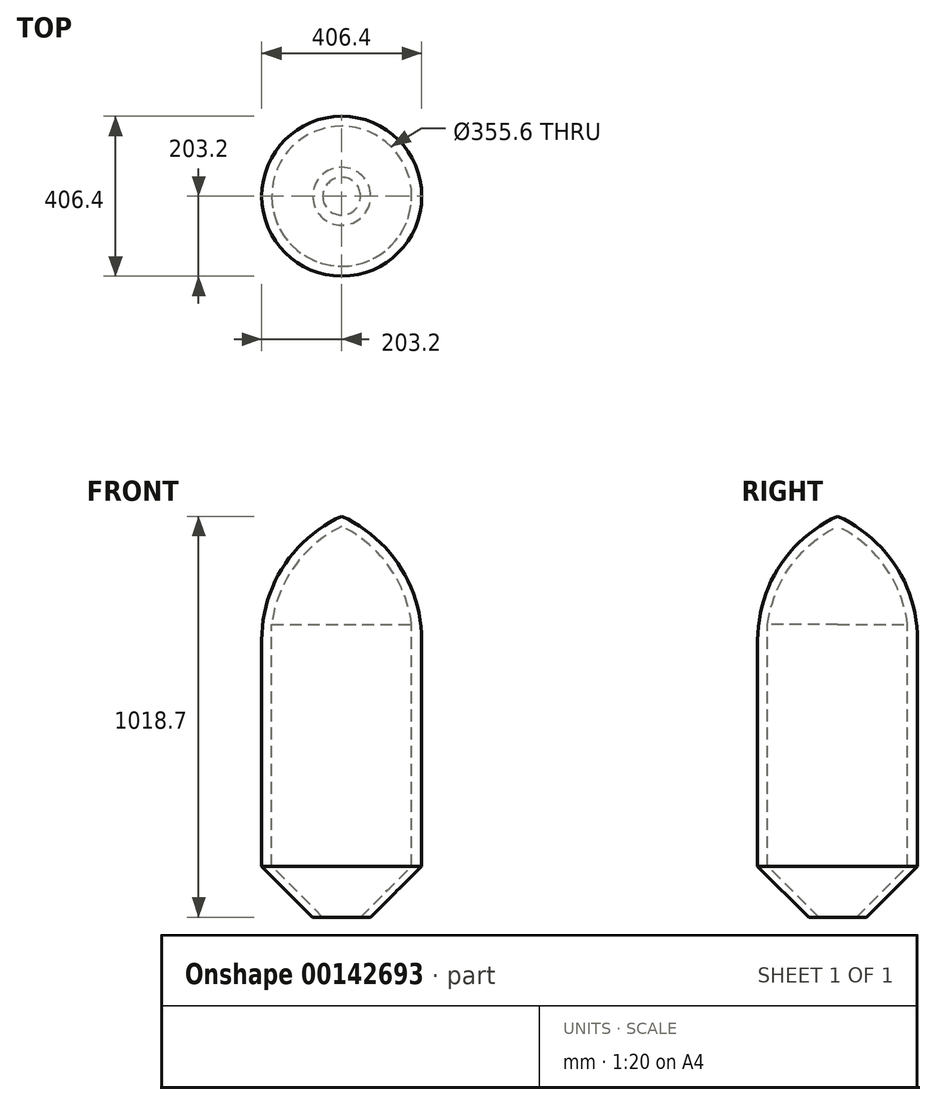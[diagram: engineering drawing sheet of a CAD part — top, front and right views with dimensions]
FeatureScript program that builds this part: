
annotation { "Feature Type Name" : "Feature", "Feature Type Description" : "" }
export const myFeature = defineFeature(function(context is Context, id is Id, definition is map)
    precondition{}
    {
        {
            var Q0;
            Q0=qCreatedBy(makeId("Front.planeOp"),FACE);
            var sketch = newSketch(context, id + "F0", { "sketchPlane" : qUnion([Q0])});
            skLineSegment(sketch, "E0", {"start": v(0, 0) * mm, "end": v(203.2, 203.2) * mm});
            skLineSegment(sketch, "E1", {"start": v(203.2, 203.2) * mm, "end": v(203.2, 777.73) * mm});
            skArc(sketch, "E2", {"start": v(203.2, 777.73) * mm, "mid": v(147.98, 964.94) * mm, "end": v(0, 1092.2) * mm});
            skArc(sketch, "E3", {"start": v(177.8, 817.07) * mm, "mid": v(120.53, 964.46) * mm, "end": v(0, 1066.8) * mm});
            skLineSegment(sketch, "E4", {"start": v(177.8, 817.07) * mm, "end": v(177.8, 203.2) * mm});
            skLineSegment(sketch, "E5", {"start": v(177.8, 203.2) * mm, "end": v(0, 25.4) * mm});
            skLineSegment(sketch, "E6", {"start": v(0, 25.4) * mm, "end": v(0, 0) * mm});
            skLineSegment(sketch, "E7", {"start": v(0, 1066.8) * mm, "end": v(0, 1092.2) * mm});
            skSolve(sketch);
        }
        {
            var Q0;
            Q0 = qSketchRegion(id + "F0", true);
            var Q1;
            Q1=sQuery(id+"F0.wireOp",EDGE,"E6");
            revolve(context, id + "F1", {"entities" : qUnion([Q0]), "axis" : qUnion([Q1]), "revolveType" : RevolveType.FULL});
        }
        {
            var Q0;
            Q0=qCreatedBy(makeId("Front.planeOp"),FACE);
            var sketch = newSketch(context, id + "F2", { "sketchPlane" : qUnion([Q0])});
            skLineSegment(sketch, "E8.bottom", {"start": v(-448.44, -51.97) * mm, "end": v(353.18, -51.97) * mm});
            skLineSegment(sketch, "E8.top", {"start": v(-448.44, 73.5) * mm, "end": v(353.18, 73.5) * mm});
            skLineSegment(sketch, "E8.left", {"start": v(-448.44, -51.97) * mm, "end": v(-448.44, 73.5) * mm});
            skLineSegment(sketch, "E8.right", {"start": v(353.18, -51.97) * mm, "end": v(353.18, 73.5) * mm});
            skSolve(sketch);
        }
        {
            var Q0;
            Q0 = qSketchRegion(id + "F2", true);
            extrude(context, id + "F3", {"entities" : qUnion([Q0]), "operationType" : NewBodyOperationType.REMOVE, "endBound" : BoundingType.THROUGH_ALL, "oppositeDirection" : true, "depth" : 25.4 * mm, "hasSecondDirection" : true, "secondDirectionBound" : SecondDirectionBoundingType.THROUGH_ALL, "secondDirectionOppositeDirection" : false, "secondDirectionDepth" : 25.4 * mm});
        }
    });
